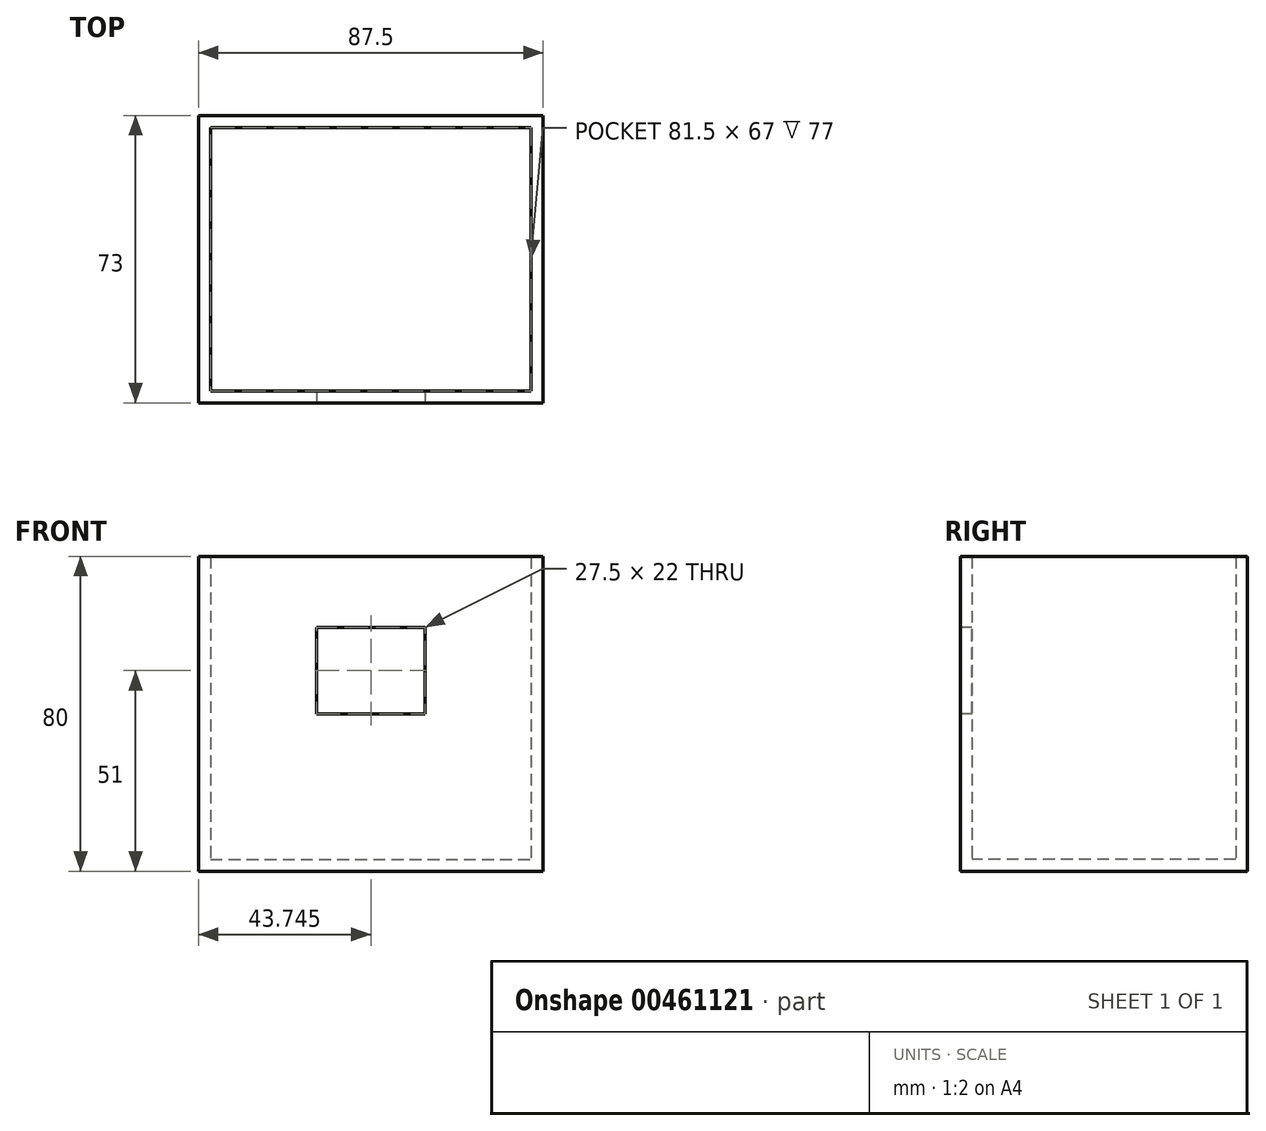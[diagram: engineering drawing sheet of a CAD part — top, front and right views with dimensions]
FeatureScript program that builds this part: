
annotation { "Feature Type Name" : "Feature", "Feature Type Description" : "" }
export const myFeature = defineFeature(function(context is Context, id is Id, definition is map)
    precondition{}
    {
        {
            var Q0;
            Q0=qCreatedBy(makeId("Top.planeOp"),FACE);
            var sketch = newSketch(context, id + "F0", { "sketchPlane" : qUnion([Q0])});
            skLineSegment(sketch, "E0.bottom", {"start": v(-472.6, -363.15) * mm, "end": v(-385.1, -363.15) * mm});
            skLineSegment(sketch, "E0.top", {"start": v(-472.6, -436.15) * mm, "end": v(-385.1, -436.15) * mm});
            skLineSegment(sketch, "E0.left", {"start": v(-472.6, -363.15) * mm, "end": v(-472.6, -436.15) * mm});
            skLineSegment(sketch, "E0.right", {"start": v(-385.1, -363.15) * mm, "end": v(-385.1, -436.15) * mm});
            skSolve(sketch);
        }
        {
            var Q0;
            Q0=makeQuery(id+"F0.imprint","IMPRINT",FACE,{"disambiguationData":[TD([[makeQuery(id+"F0.imprint","IMPRINT",EDGE,{"derivedFrom":sQuery(id+"F0.wireOp",EDGE,"E0.bottom")}),-1.0]])]});
            extrude(context, id + "F1", {"entities" : qUnion([Q0]), "depth" : 80 * mm});
        }
        {
            var Q0;
            Q0=makeQuery(id+"F1.opExtrude","CAP_FACE",FACE,{"disambiguationData":[OSD([sQuery(id+"F0.wireOp",EDGE,"E0.bottom"),sQuery(id+"F0.wireOp",EDGE,"E0.top"),sQuery(id+"F0.wireOp",EDGE,"E0.left"),sQuery(id+"F0.wireOp",EDGE,"E0.right")])],"isStart":false});
            shell(context, id + "F2", {"entities" : qUnion([Q0]), "thickness" : 3 * mm});
        }
        {
            var Q0;
            Q0=makeQuery(id+"F1.opExtrude","SWEPT_FACE",FACE,{"disambiguationData":[OSD([sQuery(id+"F0.wireOp",EDGE,"E0.top")])]});
            var sketch = newSketch(context, id + "F3", { "sketchPlane" : qUnion([Q0])});
            skLineSegment(sketch, "E1.bottom", {"start": v(-442.6, 40) * mm, "end": v(-415.1, 40) * mm});
            skLineSegment(sketch, "E1.top", {"start": v(-442.6, 62) * mm, "end": v(-415.1, 62) * mm});
            skLineSegment(sketch, "E1.left", {"start": v(-442.6, 62) * mm, "end": v(-442.6, 40) * mm});
            skLineSegment(sketch, "E1.right", {"start": v(-415.1, 62) * mm, "end": v(-415.1, 40) * mm});
            skSolve(sketch);
        }
        {
            var Q0;
            Q0 = qSketchRegion(id + "F3", true);
            extrude(context, id + "F4", {"entities" : qUnion([Q0]), "operationType" : NewBodyOperationType.REMOVE, "oppositeDirection" : true, "depth" : 3.1 * mm});
        }
    });
